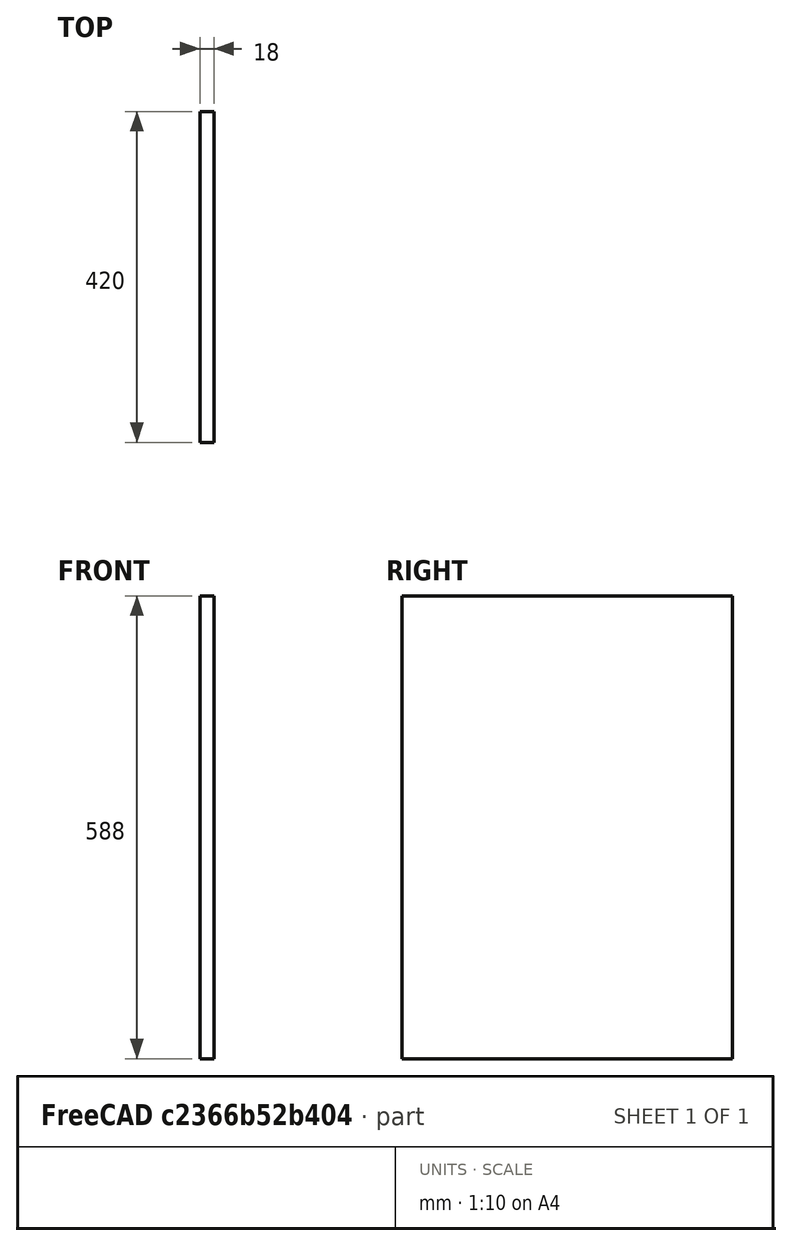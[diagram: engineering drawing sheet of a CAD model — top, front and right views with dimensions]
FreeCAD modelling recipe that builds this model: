
FCSTD DOCUMENT  (FreeCAD 0.18R4 (GitTag))
Label: divider
License: All rights reserved
LicenseURL: http://en.wikipedia.org/wiki/All_rights_reserved
objects: Sketcher::SketchObject×1, PartDesign::Pad×1, PartDesign::Body×1
note: 4 computed .brp shape members not serialized (recipe doc carries the construction recipe); baked Part::Feature solids carry a one-line shape summary decoded from their .brp

FEATURE [Sketcher::SketchObject] Sketch
  MapMode = 5
  Placement = pos=(0,0,0) rot=(0.57735,0.57735,0.57735;2.0944rad)
  Support = -> [YZ_Plane]
  sketch-geometry (4):
    g0: LineSegment StartX=0 StartY=0 StartZ=0 EndX=-420 EndY=0 EndZ=0
    g1: LineSegment StartX=-420 StartY=0 StartZ=0 EndX=-420 EndY=588 EndZ=0
    g2: LineSegment StartX=-420 StartY=588 StartZ=0 EndX=0 EndY=588 EndZ=0
    g3: LineSegment StartX=0 StartY=588 StartZ=0 EndX=0 EndY=0 EndZ=0
  constraints (11):
    c: Coincident(g0,g1)
    c: Coincident(g1,g2)
    c: Coincident(g2,g3)
    c: Coincident(g3,g0)
    c: Horizontal(g0)
    c: Horizontal(g2)
    c: Vertical(g1)
    c: Vertical(g3)
    c: Coincident(g0,g-1)
    c: DistanceX(g0,g0) = 420
    c: DistanceY(g3,g3) = 588
FEATURE [PartDesign::Pad] Pad
  Length = 18
  Length2 = 100
  Placement = pos=(0,0,0) rot=(0.57735,0.57735,0.57735;2.0944rad)
  Profile = -> Sketch
  Type = 0
FEATURE [PartDesign::Body] Body
  Group = -> [Sketch,Pad]
  Origin = -> Origin
  Tip = -> Pad
